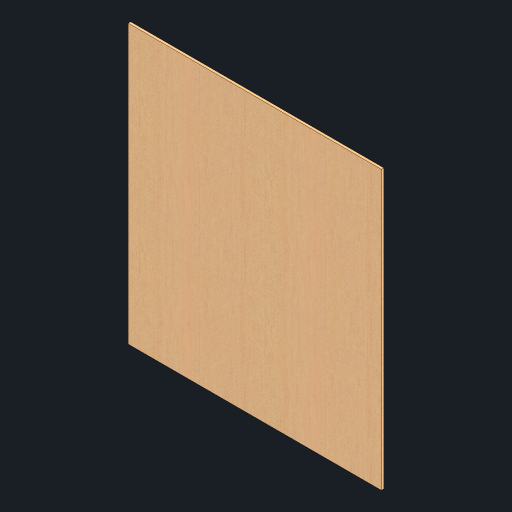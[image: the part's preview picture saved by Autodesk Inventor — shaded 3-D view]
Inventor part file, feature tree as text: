
AUTODESK INVENTOR PART (.ipt)
format: ipt  version: 2024.1 (Build 281209000, 209)  size: 242,688 bytes
history: native  units: mm
features: other x2, extrude x1, sketch x1
ambient origin geometry x8: Origin, YZ Plane, XZ Plane, XY Plane, X Axis, Y Axis, Z Axis, Center Point
bodies: Body1 (feature_tree)
feature tree (4):
  other  "솔리드1"
  extrude  "돌출1"  Depth=510.0mm
  sketch  "스케치1"
  other  "Finish1"
